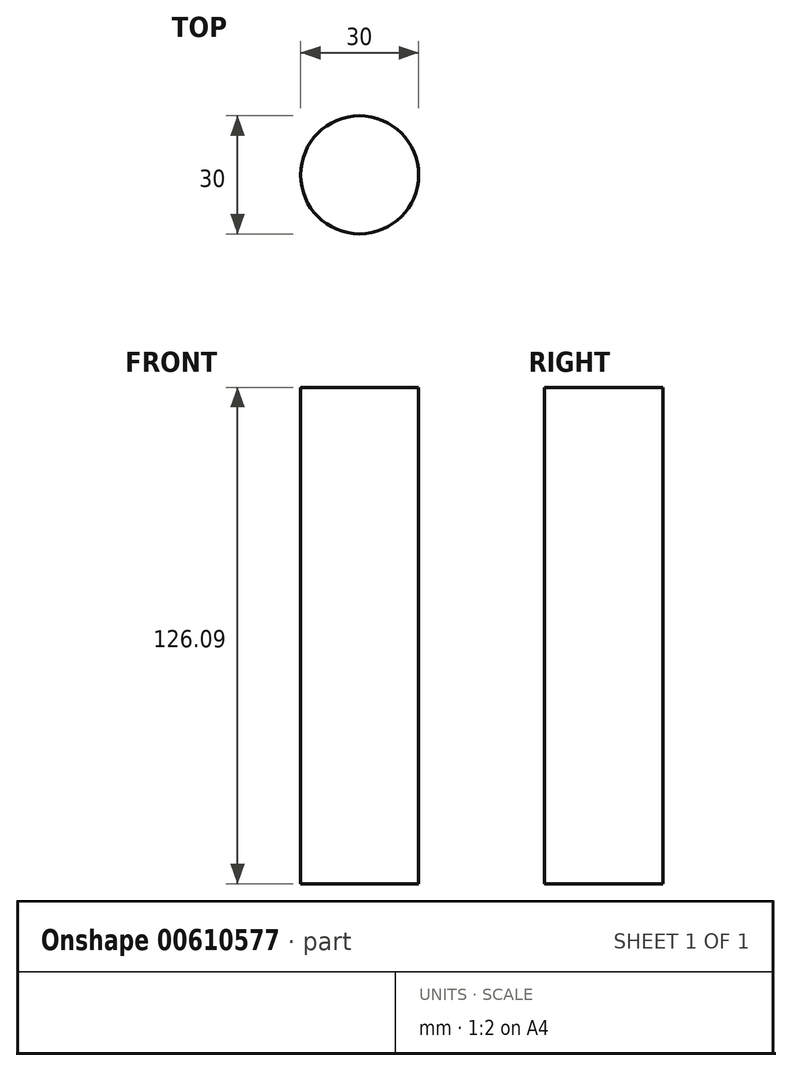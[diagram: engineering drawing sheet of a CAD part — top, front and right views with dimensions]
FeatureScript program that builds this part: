
annotation { "Feature Type Name" : "Feature", "Feature Type Description" : "" }
export const myFeature = defineFeature(function(context is Context, id is Id, definition is map)
    precondition{}
    {
        {
            var Q0;
            Q0=qCreatedBy(makeId("Top.planeOp"),FACE);
            var sketch = newSketch(context, id + "F0", { "sketchPlane" : qUnion([Q0])});
            skCircle(sketch, "E0", {"center": v(0, 0) * mm, "radius": 15 * mm});
            skSolve(sketch);
        }
        {
            var Q0;
            Q0=makeQuery(id+"F0.imprint","IMPRINT",FACE,{"disambiguationData":[TD([[makeQuery(id+"F0.imprint","IMPRINT",EDGE,{"derivedFrom":sQuery(id+"F0.wireOp",EDGE,"E0")}),1.0]])]});
            extrude(context, id + "F1", {"entities" : qUnion([Q0]), "depth" : 126.1 * mm, "offsetDistance" : 25.4 * mm});
        }
    });
